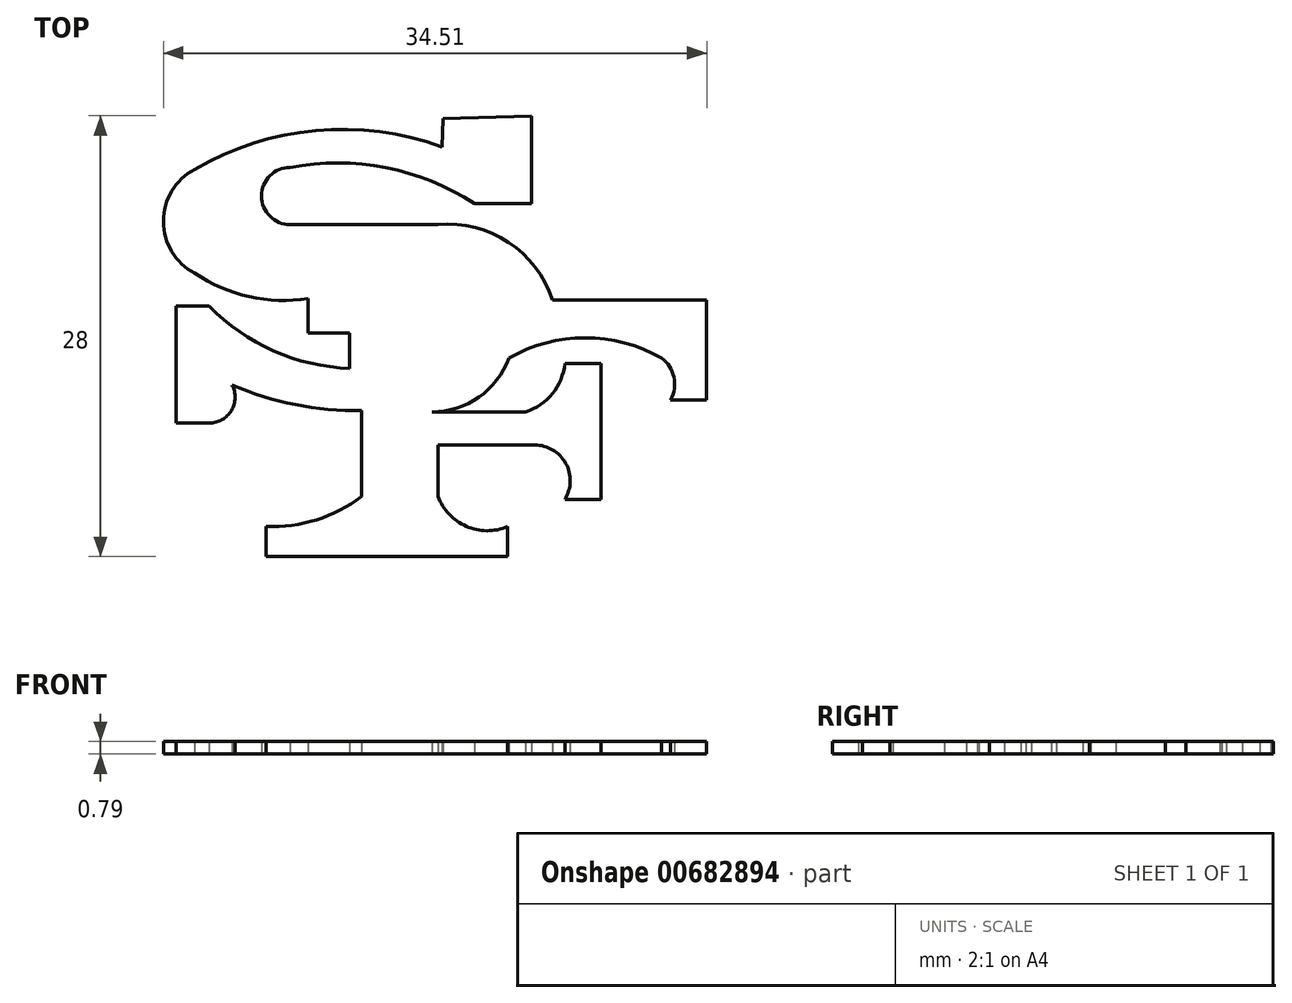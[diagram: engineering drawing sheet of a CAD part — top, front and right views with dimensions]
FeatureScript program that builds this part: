
annotation { "Feature Type Name" : "Feature", "Feature Type Description" : "" }
export const myFeature = defineFeature(function(context is Context, id is Id, definition is map)
    precondition{}
    {
        {
            var Q0;
            Q0=qCreatedBy(makeId("Top.planeOp"),FACE);
            var sketch = newSketch(context, id + "F0", { "sketchPlane" : qUnion([Q0])});
            skArc(sketch, "E0", {"start": v(41.94, -25.58) * mm, "mid": v(33.92, -24.53) * mm, "end": v(26.22, -27) * mm});
            skArc(sketch, "E1", {"start": v(26.22, -27) * mm, "mid": v(24.24, -30.3) * mm, "end": v(26.22, -33.6) * mm});
            skArc(sketch, "E2", {"start": v(26.22, -33.6) * mm, "mid": v(29.68, -35.08) * mm, "end": v(33.44, -35.21) * mm});
            skArc(sketch, "E3", {"start": v(27.15, -35.7) * mm, "mid": v(31.23, -38.53) * mm, "end": v(36.08, -39.64) * mm});
            skLineSegment(sketch, "E4", {"start": v(27.15, -35.7) * mm, "end": v(25.05, -35.7) * mm});
            skLineSegment(sketch, "E5", {"start": v(25.05, -35.7) * mm, "end": v(25.05, -43.11) * mm});
            skLineSegment(sketch, "E6", {"start": v(25.05, -43.11) * mm, "end": v(27.15, -43.11) * mm});
            skArc(sketch, "E7", {"start": v(27.15, -43.11) * mm, "mid": v(28.56, -42.31) * mm, "end": v(28.6, -40.7) * mm});
            skArc(sketch, "E8", {"start": v(28.6, -40.7) * mm, "mid": v(32.62, -41.95) * mm, "end": v(36.82, -42.3) * mm});
            skLineSegment(sketch, "E9", {"start": v(36.82, -42.3) * mm, "end": v(36.82, -47.79) * mm});
            skArc(sketch, "E10", {"start": v(30.76, -49.69) * mm, "mid": v(33.95, -49.26) * mm, "end": v(36.82, -47.79) * mm});
            skLineSegment(sketch, "E11", {"start": v(30.76, -49.69) * mm, "end": v(30.76, -51.6) * mm});
            skLineSegment(sketch, "E12", {"start": v(30.76, -51.6) * mm, "end": v(46.1, -51.6) * mm});
            skLineSegment(sketch, "E13", {"start": v(46.1, -51.6) * mm, "end": v(46.1, -49.7) * mm});
            skArc(sketch, "E14", {"start": v(41.68, -47.77) * mm, "mid": v(43.48, -49.67) * mm, "end": v(46.1, -49.7) * mm});
            skLineSegment(sketch, "E15", {"start": v(41.68, -47.77) * mm, "end": v(41.68, -44.51) * mm});
            skLineSegment(sketch, "E16", {"start": v(41.68, -44.51) * mm, "end": v(47.82, -44.51) * mm});
            skArc(sketch, "E17", {"start": v(49.74, -47.96) * mm, "mid": v(49.8, -45.67) * mm, "end": v(47.82, -44.51) * mm});
            skLineSegment(sketch, "E18", {"start": v(52.04, -47.96) * mm, "end": v(52.04, -39.33) * mm});
            skLineSegment(sketch, "E19", {"start": v(52.04, -39.33) * mm, "end": v(49.74, -39.33) * mm});
            skArc(sketch, "E20", {"start": v(47.24, -42.4) * mm, "mid": v(48.95, -41.24) * mm, "end": v(49.74, -39.33) * mm});
            skLineSegment(sketch, "E21", {"start": v(47.24, -42.4) * mm, "end": v(41.3, -42.4) * mm});
            skArc(sketch, "E22", {"start": v(55.87, -38.99) * mm, "mid": v(51.02, -37.7) * mm, "end": v(46.18, -38.99) * mm});
            skArc(sketch, "E23", {"start": v(56.45, -41.63) * mm, "mid": v(56.66, -40.2) * mm, "end": v(55.87, -38.99) * mm});
            skLineSegment(sketch, "E24", {"start": v(56.45, -41.63) * mm, "end": v(58.75, -41.63) * mm});
            skLineSegment(sketch, "E25", {"start": v(58.75, -41.63) * mm, "end": v(58.75, -35.3) * mm});
            skLineSegment(sketch, "E26", {"start": v(58.75, -35.3) * mm, "end": v(48.95, -35.3) * mm});
            skPoint(sketch, "E26.endSnap0", {"position": v(48.95, -41.24) * mm});
            skArc(sketch, "E27", {"start": v(48.95, -35.3) * mm, "mid": v(46.16, -31.64) * mm, "end": v(41.68, -30.51) * mm});
            skLineSegment(sketch, "E28", {"start": v(41.68, -30.51) * mm, "end": v(32.3, -30.51) * mm});
            skArc(sketch, "E29", {"start": v(32.3, -26.87) * mm, "mid": v(30.47, -28.7) * mm, "end": v(32.3, -30.51) * mm});
            skArc(sketch, "E30", {"start": v(43.99, -29.17) * mm, "mid": v(38.36, -26.9) * mm, "end": v(32.3, -26.87) * mm});
            skLineSegment(sketch, "E31", {"start": v(43.99, -29.17) * mm, "end": v(47.63, -29.17) * mm});
            skLineSegment(sketch, "E32", {"start": v(41.94, -25.58) * mm, "end": v(42, -23.76) * mm});
            skLineSegment(sketch, "E33", {"start": v(47.63, -29.17) * mm, "end": v(47.63, -23.6) * mm});
            skLineSegment(sketch, "E34", {"start": v(47.63, -23.6) * mm, "end": v(42, -23.76) * mm});
            skLineSegment(sketch, "E35", {"start": v(33.44, -35.21) * mm, "end": v(33.44, -37.38) * mm});
            skLineSegment(sketch, "E36", {"start": v(33.44, -37.38) * mm, "end": v(36.08, -37.38) * mm});
            skLineSegment(sketch, "E37", {"start": v(36.08, -37.38) * mm, "end": v(36.08, -39.64) * mm});
            skPoint(sketch, "E38.end.orphan", {"position": v(41.66, -35.21) * mm});
            skPoint(sketch, "E38.start.orphan", {"position": v(41.66, -38.6) * mm});
            skLineSegment(sketch, "E39", {"start": v(49.74, -47.96) * mm, "end": v(52.04, -47.96) * mm});
            skArc(sketch, "E40", {"start": v(41.3, -42.4) * mm, "mid": v(44.28, -41.46) * mm, "end": v(46.18, -38.99) * mm});
            skSolve(sketch);
        }
        {
            var Q0;
            Q0=makeQuery(id+"F0.imprint","IMPRINT",FACE,{"disambiguationData":[TD([[makeQuery(id+"F0.imprint","IMPRINT",EDGE,{"derivedFrom":sQuery(id+"F0.wireOp",EDGE,"E0")}),1.0]])]});
            extrude(context, id + "F1", {"entities" : qUnion([Q0]), "depth" : 0.8 * mm, "offsetDistance" : 25.4 * mm});
        }
    });
